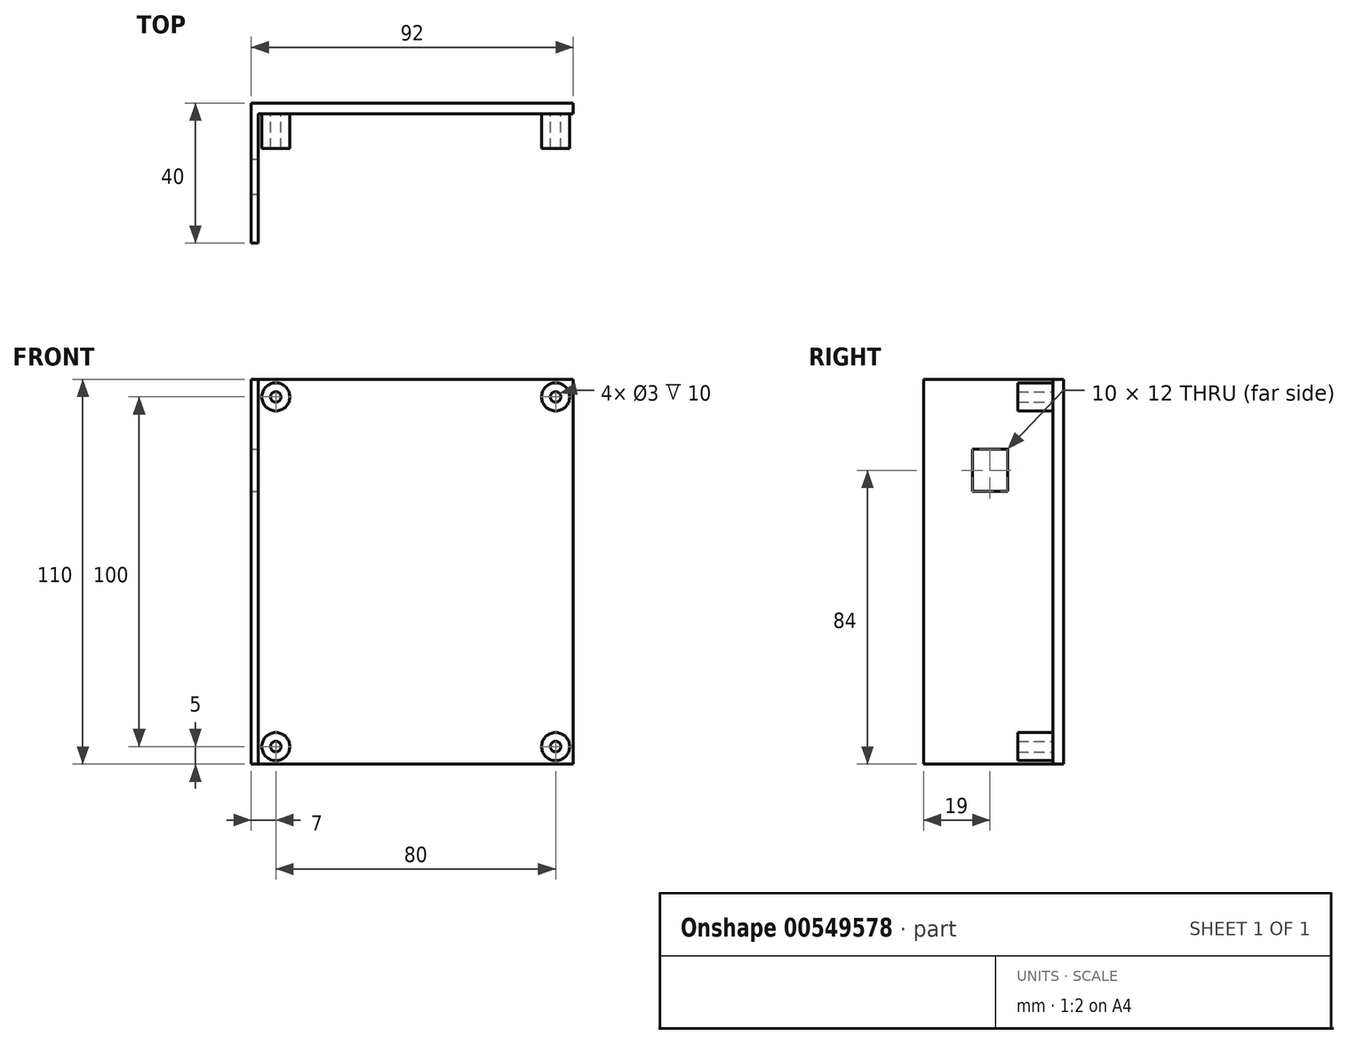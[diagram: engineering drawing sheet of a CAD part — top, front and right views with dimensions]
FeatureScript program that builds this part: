
annotation { "Feature Type Name" : "Feature", "Feature Type Description" : "" }
export const myFeature = defineFeature(function(context is Context, id is Id, definition is map)
    precondition{}
    {
        {
            var Q0;
            Q0=qCreatedBy(makeId("Front.planeOp"),FACE);
            var sketch = newSketch(context, id + "F0", { "sketchPlane" : qUnion([Q0])});
            skLineSegment(sketch, "E0.bottom", {"start": v(-45, 55) * mm, "end": v(45, 55) * mm});
            skLineSegment(sketch, "E0.top", {"start": v(-45, -55) * mm, "end": v(45, -55) * mm});
            skLineSegment(sketch, "E0.left", {"start": v(-45, 55) * mm, "end": v(-45, -55) * mm});
            skLineSegment(sketch, "E0.right", {"start": v(45, 55) * mm, "end": v(45, -55) * mm});
            skSolve(sketch);
        }
        {
            var Q0;
            Q0=qSketchRegion(id+"F0",true);
            extrude(context, id + "F1", {"entities" : qUnion([Q0]), "oppositeDirection" : true, "depth" : 3 * mm, "offsetDistance" : 25 * mm});
        }
        {
            var Q0;
            Q0=makeQuery(id+"F1.opExtrude","CAP_FACE",FACE,{"disambiguationData":[OSD([sQuery(id+"F0.wireOp",EDGE,"E0.bottom"),sQuery(id+"F0.wireOp",EDGE,"E0.top"),sQuery(id+"F0.wireOp",EDGE,"E0.left"),sQuery(id+"F0.wireOp",EDGE,"E0.right")])],"isStart":true});
            var sketch = newSketch(context, id + "F2", { "sketchPlane" : qUnion([Q0])});
            skLineSegment(sketch, "E1.bottom", {"start": v(-40, 50) * mm, "end": v(40, 50) * mm, "construction": true});
            skLineSegment(sketch, "E1.top", {"start": v(-40, -50) * mm, "end": v(40, -50) * mm, "construction": true});
            skLineSegment(sketch, "E1.left", {"start": v(-40, 50) * mm, "end": v(-40, -50) * mm, "construction": true});
            skLineSegment(sketch, "E1.right", {"start": v(40, 50) * mm, "end": v(40, -50) * mm, "construction": true});
            skCircle(sketch, "E2", {"center": v(-40, 50) * mm, "radius": 1.5 * mm});
            skCircle(sketch, "E3", {"center": v(40, 50) * mm, "radius": 1.5 * mm});
            skCircle(sketch, "E4", {"center": v(40, 50) * mm, "radius": 4 * mm});
            skCircle(sketch, "E5", {"center": v(-40, 50) * mm, "radius": 4 * mm});
            skCircle(sketch, "E6", {"center": v(-40, -50) * mm, "radius": 1.5 * mm});
            skCircle(sketch, "E7", {"center": v(-40, -50) * mm, "radius": 4 * mm});
            skCircle(sketch, "E8", {"center": v(40, -50) * mm, "radius": 4 * mm});
            skCircle(sketch, "E9", {"center": v(40, -50) * mm, "radius": 1.5 * mm});
            skSolve(sketch);
        }
        {
            var Q0;
            Q0=qSketchRegion(id+"F2",true);
            extrude(context, id + "F3", {"entities" : qUnion([Q0]), "operationType" : NewBodyOperationType.ADD, "depth" : 10 * mm, "offsetDistance" : 25 * mm});
        }
        {
            var Q0;
            Q0=makeQuery(id+"F1.opExtrude","SWEPT_FACE",FACE,{"disambiguationData":[OSD([sQuery(id+"F0.wireOp",EDGE,"E0.left")])]});
            var sketch = newSketch(context, id + "F4", { "sketchPlane" : qUnion([Q0])});
            skLineSegment(sketch, "E10.bottom", {"start": v(-3, 55) * mm, "end": v(37, 55) * mm});
            skLineSegment(sketch, "E10.top", {"start": v(-3, -55) * mm, "end": v(37, -55) * mm});
            skLineSegment(sketch, "E10.left", {"start": v(-3, 55) * mm, "end": v(-3, -55) * mm});
            skLineSegment(sketch, "E10.right", {"start": v(37, 55) * mm, "end": v(37, -55) * mm});
            skLineSegment(sketch, "E11.bottom", {"start": v(13, 35) * mm, "end": v(23, 35) * mm});
            skLineSegment(sketch, "E11.top", {"start": v(13, 23) * mm, "end": v(23, 23) * mm});
            skLineSegment(sketch, "E11.left", {"start": v(13, 35) * mm, "end": v(13, 23) * mm});
            skLineSegment(sketch, "E11.right", {"start": v(23, 35) * mm, "end": v(23, 23) * mm});
            skSolve(sketch);
        }
        {
            var Q0;
            Q0=qSketchRegion(id+"F4",true);
            extrude(context, id + "F5", {"entities" : qUnion([Q0]), "operationType" : NewBodyOperationType.ADD, "depth" : 2 * mm, "offsetDistance" : 25 * mm});
        }
    });
